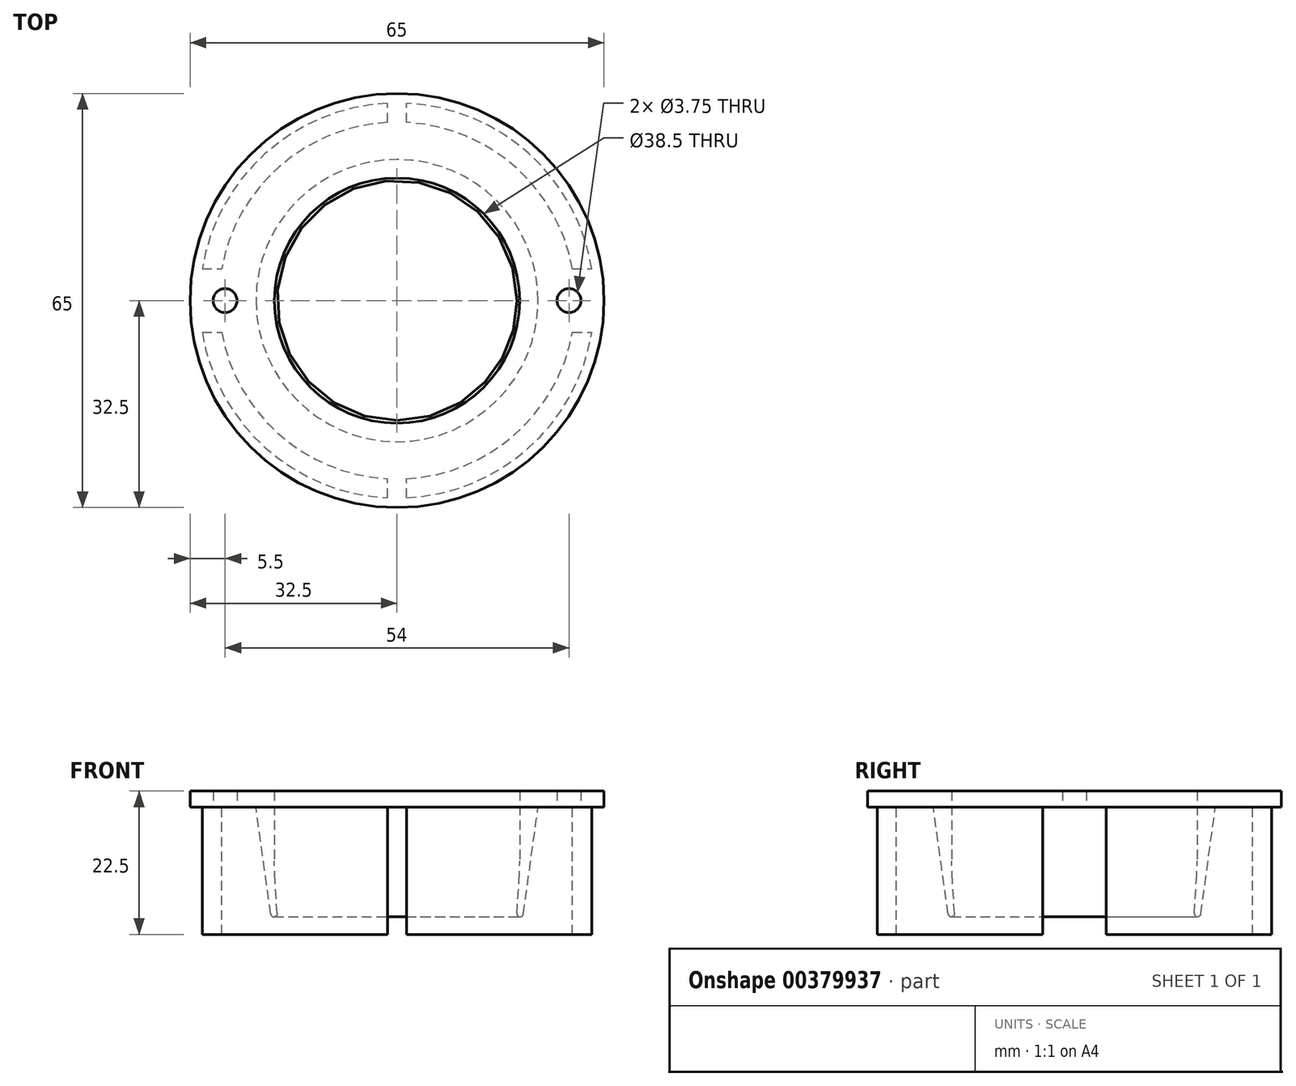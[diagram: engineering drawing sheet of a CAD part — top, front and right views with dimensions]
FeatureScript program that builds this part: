
annotation { "Feature Type Name" : "Feature", "Feature Type Description" : "" }
export const myFeature = defineFeature(function(context is Context, id is Id, definition is map)
    precondition{}
    {
        {
            var Q0;
            Q0=qCreatedBy(makeId("Front.planeOp"),FACE);
            var sketch = newSketch(context, id + "F0", { "sketchPlane" : qUnion([Q0])});
            skLineSegment(sketch, "E0", {"start": v(0, 0) * mm, "end": v(0, 10) * mm, "construction": true});
            skLineSegment(sketch, "E1", {"start": v(-22.15, 10) * mm, "end": v(-18, -20) * mm});
            skLineSegment(sketch, "E2", {"start": v(-22.15, 10) * mm, "end": v(-19.25, 10) * mm});
            skLineSegment(sketch, "E3", {"start": v(-19.25, 10) * mm, "end": v(-19.25, 0) * mm});
            skLineSegment(sketch, "E4", {"start": v(-19.25, 0) * mm, "end": v(-18, -20) * mm});
            skLineSegment(sketch, "E5", {"start": v(-19.25, 0) * mm, "end": v(0, 0) * mm, "construction": true});
            skSolve(sketch);
        }
        {
            var Q0;
            Q0=makeQuery(id+"F0.imprint","IMPRINT",FACE,{"disambiguationData":[TD([[makeQuery(id+"F0.imprint","IMPRINT",EDGE,{"derivedFrom":sQuery(id+"F0.wireOp",EDGE,"E1")}),1.0]])]});
            var Q1;
            Q1=sQuery(id+"F0.wireOp",EDGE,"E0");
            revolve(context, id + "F1", {"entities" : qUnion([Q0]), "axis" : qUnion([Q1]), "revolveType" : RevolveType.FULL});
        }
        {
            var Q0;
            Q0=makeQuery(id+"F1.opRevolve","SWEPT_EDGE",EDGE,{"disambiguationData":[OSD([sQuery(id+"F0.wireOp",EDGE,"E1"),sQuery(id+"F0.wireOp",EDGE,"E4")])]});
            fillet(context, id + "F2", {"entities" : qUnion([Q0]), "radius" : .5 * mm, "tangentPropagation" : true, "allowEdgeOverflow" : false});
        }
        {
            var Q0;
            Q0=makeQuery(id+"F1.opRevolve","SWEPT_FACE",FACE,{"disambiguationData":[OSD([sQuery(id+"F0.wireOp",EDGE,"E2")])]});
            var sketch = newSketch(context, id + "F3", { "sketchPlane" : qUnion([Q0])});
            skCircle(sketch, "E6", {"center": v(0, 0) * mm, "radius": 19.25 * mm});
            skCircle(sketch, "E7", {"center": v(-27, 0) * mm, "radius": 1.88 * mm});
            skCircle(sketch, "E8", {"center": v(27, 0) * mm, "radius": 1.88 * mm});
            skLineSegment(sketch, "E9", {"start": v(0, 0) * mm, "end": v(-27, 0) * mm, "construction": true});
            skLineSegment(sketch, "E10", {"start": v(0, 0) * mm, "end": v(27, 0) * mm, "construction": true});
            skCircle(sketch, "E11", {"center": v(0, 0) * mm, "radius": 32.5 * mm});
            skSolve(sketch);
        }
        {
            var Q0;
            Q0=makeQuery(id+"F3.imprint","IMPRINT",FACE,{"disambiguationData":[TD([[makeQuery(id+"F3.imprint","IMPRINT",EDGE,{"derivedFrom":sQuery(id+"F3.wireOp",EDGE,"E7")}),-1.0]])]});
            var Q1;
            Q1=makeQuery(id+"F3.imprint","IMPRINT",FACE,{"disambiguationData":[TD([[makeQuery(id+"F3.imprint","IMPRINT",EDGE,{"derivedFrom":sQuery(id+"F3.wireOp",EDGE,"E6")}),1.0]])]});
            extrude(context, id + "F4", {"entities" : qUnion([Q0, Q1]), "operationType" : NewBodyOperationType.ADD, "depth" : 2.5 * mm});
        }
        {
            var Q0;
            Q0=makeQuery(id+"F4.opExtrude","CAP_FACE",FACE,{"disambiguationData":[OSD([sQuery(id+"F3.wireOp",EDGE,"E6"),sQuery(id+"F3.wireOp",EDGE,"E7"),sQuery(id+"F3.wireOp",EDGE,"E8"),sQuery(id+"F3.wireOp",EDGE,"E11")])],"isStart":true});
            var sketch = newSketch(context, id + "F5", { "sketchPlane" : qUnion([Q0])});
            skArc(sketch, "E12", {"start": v(-1.5, 27.96) * mm, "mid": v(-18.51, 21) * mm, "end": v(-27.55, 5) * mm});
            skArc(sketch, "E13", {"start": v(-1.5, 30.96) * mm, "mid": v(-20.64, 23.13) * mm, "end": v(-30.6, 5) * mm});
            skLineSegment(sketch, "E14", {"start": v(-1.5, 30.96) * mm, "end": v(-1.5, 27.96) * mm});
            skLineSegment(sketch, "E15", {"start": v(1.5, 30.96) * mm, "end": v(1.5, 27.96) * mm});
            skLineSegment(sketch, "E16", {"start": v(-1.5, 0) * mm, "end": v(1.5, 0) * mm, "construction": true});
            skLineSegment(sketch, "E17.trimOffspring", {"start": v(1.5, -27.96) * mm, "end": v(1.5, -30.96) * mm});
            skLineSegment(sketch, "E18.trimOffspring", {"start": v(-1.5, -27.96) * mm, "end": v(-1.5, -30.96) * mm});
            skArc(sketch, "E19.trimOffspring", {"start": v(1.5, -27.96) * mm, "mid": v(18.51, -21) * mm, "end": v(27.55, -5) * mm});
            skArc(sketch, "E20.trimOffspring", {"start": v(1.5, -30.96) * mm, "mid": v(20.64, -23.13) * mm, "end": v(30.6, -5) * mm});
            skLineSegment(sketch, "E21", {"start": v(-30.6, 5) * mm, "end": v(-27.55, 5) * mm});
            skLineSegment(sketch, "E22", {"start": v(-30.6, -5) * mm, "end": v(-27.55, -5) * mm});
            skLineSegment(sketch, "E23", {"start": v(0, 5) * mm, "end": v(0, -5) * mm, "construction": true});
            skArc(sketch, "E24.trimOffspring", {"start": v(-30.6, -5) * mm, "mid": v(-20.64, -23.13) * mm, "end": v(-1.5, -30.96) * mm});
            skArc(sketch, "E25.trimOffspring", {"start": v(-27.55, -5) * mm, "mid": v(-18.51, -21) * mm, "end": v(-1.5, -27.96) * mm});
            skLineSegment(sketch, "E26.trimOffspring", {"start": v(27.55, 5) * mm, "end": v(30.6, 5) * mm});
            skLineSegment(sketch, "E27.trimOffspring", {"start": v(27.55, -5) * mm, "end": v(30.6, -5) * mm});
            skArc(sketch, "E28.trimOffspring", {"start": v(30.6, 5) * mm, "mid": v(20.64, 23.13) * mm, "end": v(1.5, 30.96) * mm});
            skArc(sketch, "E29.trimOffspring", {"start": v(27.55, 5) * mm, "mid": v(18.51, 21) * mm, "end": v(1.5, 27.96) * mm});
            skSolve(sketch);
        }
        {
            var Q0;
            Q0=makeQuery(id+"F5.imprint","IMPRINT",FACE,{"disambiguationData":[TD([[makeQuery(id+"F5.imprint","IMPRINT",EDGE,{"derivedFrom":sQuery(id+"F5.wireOp",EDGE,"E12")}),-1.0]])]});
            var Q1;
            Q1=makeQuery(id+"F5.imprint","IMPRINT",FACE,{"disambiguationData":[TD([[makeQuery(id+"F5.imprint","IMPRINT",EDGE,{"derivedFrom":sQuery(id+"F5.wireOp",EDGE,"E15")}),1.0]])]});
            var Q2;
            Q2=makeQuery(id+"F5.imprint","IMPRINT",FACE,{"disambiguationData":[TD([[makeQuery(id+"F5.imprint","IMPRINT",EDGE,{"derivedFrom":sQuery(id+"F5.wireOp",EDGE,"E17.trimOffspring")}),1.0]])]});
            var Q3;
            Q3=makeQuery(id+"F5.imprint","IMPRINT",FACE,{"disambiguationData":[TD([[makeQuery(id+"F5.imprint","IMPRINT",EDGE,{"derivedFrom":sQuery(id+"F5.wireOp",EDGE,"E18.trimOffspring")}),-1.0]])]});
            extrude(context, id + "F6", {"entities" : qUnion([Q0, Q1, Q2, Q3]), "operationType" : NewBodyOperationType.ADD, "depth" : 20 * mm});
        }
        {
            var Q0;
            Q0=makeQuery(id+"F1.opRevolve","SWEPT_EDGE",EDGE,{"disambiguationData":[OSD([sQuery(id+"F0.wireOp",EDGE,"E3"),sQuery(id+"F0.wireOp",EDGE,"E4")])]});
            fillet(context, id + "F7", {"entities" : qUnion([Q0]), "radius" : 50 * mm, "tangentPropagation" : true, "allowEdgeOverflow" : false});
        }
    });
